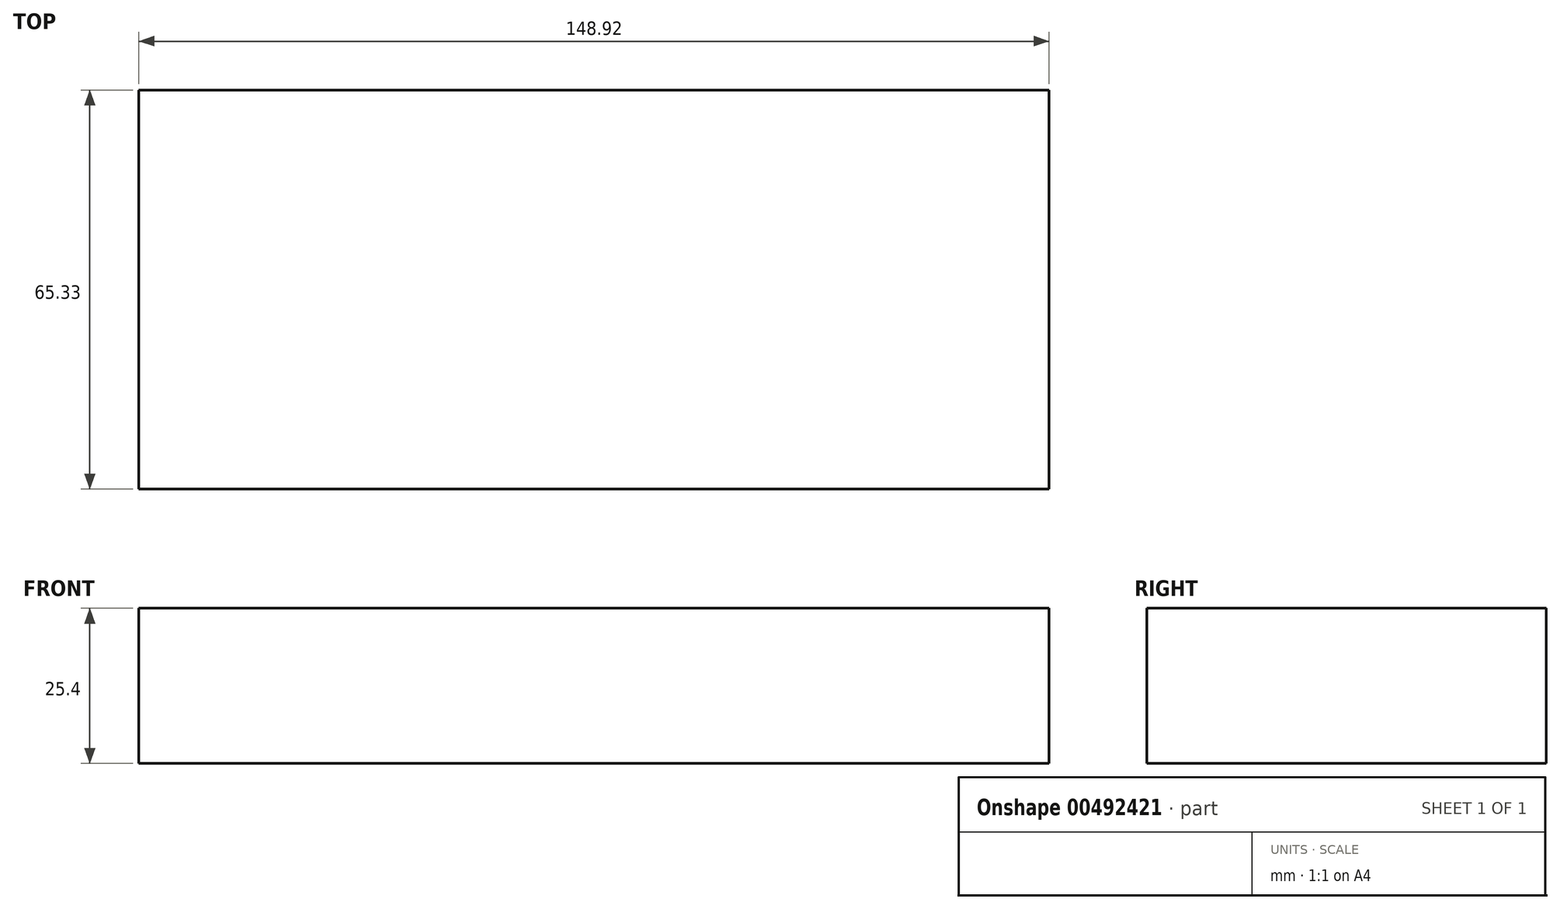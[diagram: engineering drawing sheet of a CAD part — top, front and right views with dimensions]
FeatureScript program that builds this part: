
annotation { "Feature Type Name" : "Feature", "Feature Type Description" : "" }
export const myFeature = defineFeature(function(context is Context, id is Id, definition is map)
    precondition{}
    {
        {
            var Q0;
            Q0=qCreatedBy(makeId("Top.planeOp"),FACE);
            var sketch = newSketch(context, id + "F0", { "sketchPlane" : qUnion([Q0])});
            skLineSegment(sketch, "E0.bottom", {"start": v(-106.28, 12.9) * mm, "end": v(42.64, 12.9) * mm});
            skLineSegment(sketch, "E0.top", {"start": v(-106.28, -52.43) * mm, "end": v(42.64, -52.43) * mm});
            skLineSegment(sketch, "E0.left", {"start": v(-106.28, 12.9) * mm, "end": v(-106.28, -52.43) * mm});
            skLineSegment(sketch, "E0.right", {"start": v(42.64, 12.9) * mm, "end": v(42.64, -52.43) * mm});
            skSolve(sketch);
        }
        {
            var Q0;
            Q0=makeQuery(id+"F0.imprint","IMPRINT",FACE,{"disambiguationData":[TD([[makeQuery(id+"F0.imprint","IMPRINT",EDGE,{"derivedFrom":sQuery(id+"F0.wireOp",EDGE,"E0.bottom")}),-1.0]])]});
            extrude(context, id + "F1", {"entities" : qUnion([Q0]), "depth" : 25.4 * mm});
        }
    });
